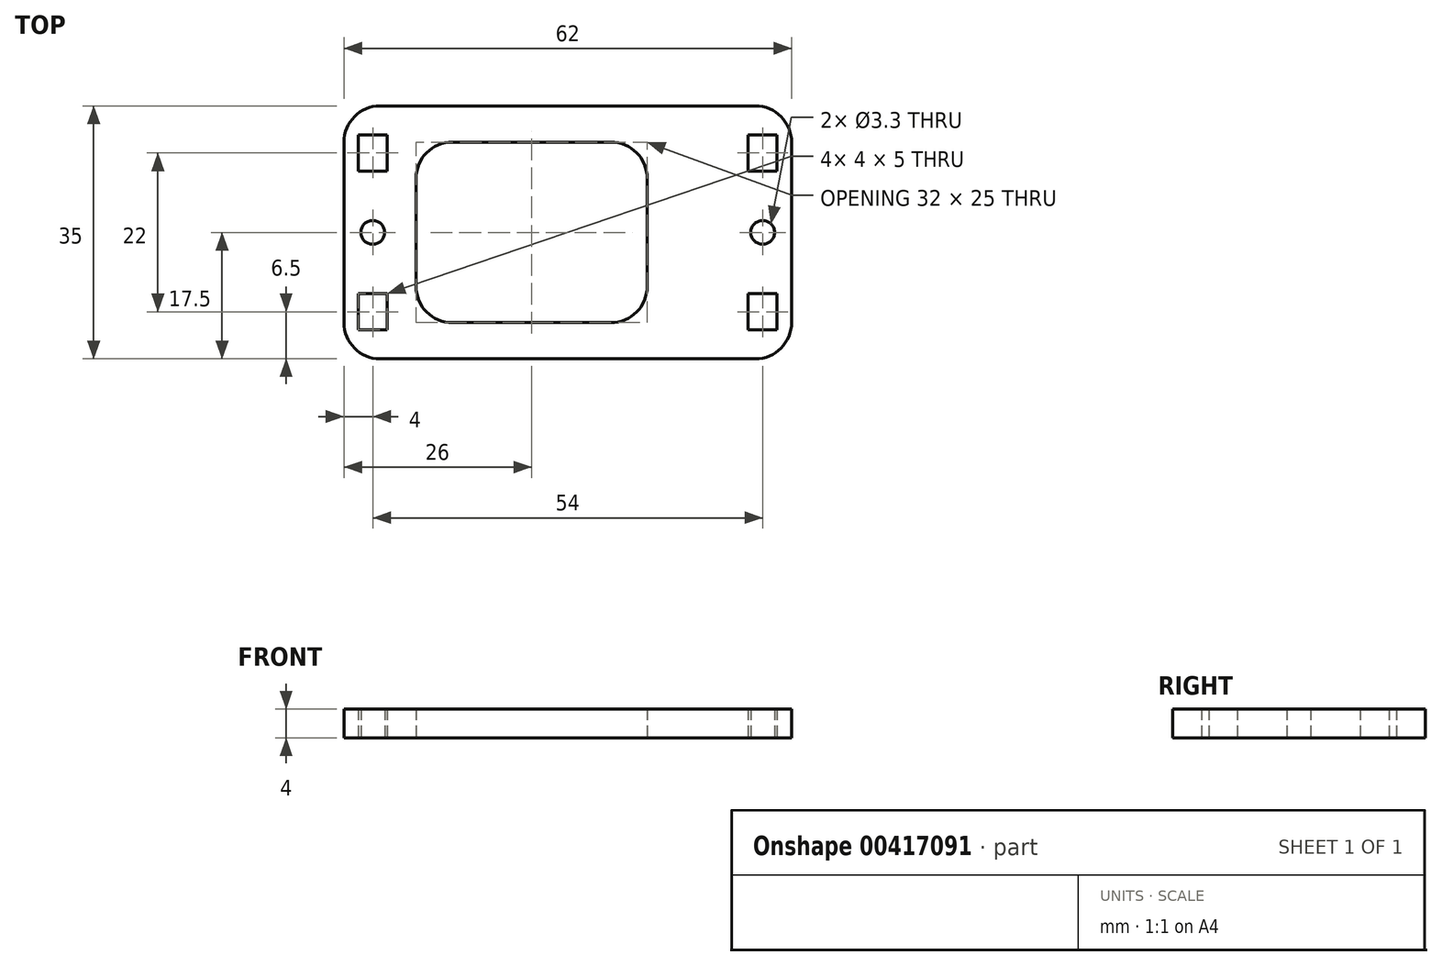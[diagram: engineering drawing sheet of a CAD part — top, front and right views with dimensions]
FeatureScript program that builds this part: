
annotation { "Feature Type Name" : "Feature", "Feature Type Description" : "" }
export const myFeature = defineFeature(function(context is Context, id is Id, definition is map)
    precondition{}
    {
        {
            var Q0;
            Q0=qCreatedBy(makeId("Top.planeOp"),FACE);
            var sketch = newSketch(context, id + "F0", { "sketchPlane" : qUnion([Q0])});
            skLineSegment(sketch, "E0.bottom", {"start": v(31, -17.5) * mm, "end": v(-31, -17.5) * mm});
            skLineSegment(sketch, "E0.top", {"start": v(31, 17.5) * mm, "end": v(-31, 17.5) * mm});
            skLineSegment(sketch, "E0.left", {"start": v(31, -17.5) * mm, "end": v(31, 17.5) * mm});
            skLineSegment(sketch, "E0.right", {"start": v(-31, -17.5) * mm, "end": v(-31, 17.5) * mm});
            skPoint(sketch, "E0.middle", {"position": v(0, 0) * mm});
            skLineSegment(sketch, "E1.bottom", {"start": v(-25, 8.5) * mm, "end": v(-29, 8.5) * mm});
            skLineSegment(sketch, "E1.top", {"start": v(-25, 13.5) * mm, "end": v(-29, 13.5) * mm});
            skLineSegment(sketch, "E1.left", {"start": v(-25, 8.5) * mm, "end": v(-25, 13.5) * mm});
            skLineSegment(sketch, "E1.right", {"start": v(-29, 8.5) * mm, "end": v(-29, 13.5) * mm});
            skPoint(sketch, "E1.middle", {"position": v(-27, 11) * mm});
            skLineSegment(sketch, "E2.MirrorCS", {"start": v(-29, -8.5) * mm, "end": v(-29, -13.5) * mm});
            skLineSegment(sketch, "E3.MirrorCS", {"start": v(-25, -8.5) * mm, "end": v(-25, -13.5) * mm});
            skLineSegment(sketch, "E4.MirrorCS", {"start": v(-25, -8.5) * mm, "end": v(-29, -8.5) * mm});
            skLineSegment(sketch, "E5.MirrorCS", {"start": v(-25, -13.5) * mm, "end": v(-29, -13.5) * mm});
            skPoint(sketch, "E6.MirrorP", {"position": v(-27, -11) * mm});
            skPoint(sketch, "E7.MirrorP", {"position": v(27, 11) * mm});
            skPoint(sketch, "E8.MirrorP", {"position": v(27, -11) * mm});
            skLineSegment(sketch, "E9.MirrorCS", {"start": v(25, -13.5) * mm, "end": v(29, -13.5) * mm});
            skLineSegment(sketch, "E10.MirrorCS", {"start": v(25, -8.5) * mm, "end": v(29, -8.5) * mm});
            skLineSegment(sketch, "E11.MirrorCS", {"start": v(25, -8.5) * mm, "end": v(25, -13.5) * mm});
            skLineSegment(sketch, "E12.MirrorCS", {"start": v(25, 8.5) * mm, "end": v(29, 8.5) * mm});
            skLineSegment(sketch, "E13.MirrorCS", {"start": v(29, -8.5) * mm, "end": v(29, -13.5) * mm});
            skLineSegment(sketch, "E14.MirrorCS", {"start": v(29, 8.5) * mm, "end": v(29, 13.5) * mm});
            skLineSegment(sketch, "E15.MirrorCS", {"start": v(25, 8.5) * mm, "end": v(25, 13.5) * mm});
            skLineSegment(sketch, "E16.MirrorCS", {"start": v(25, 13.5) * mm, "end": v(29, 13.5) * mm});
            skPoint(sketch, "E17", {"position": v(-27, 0) * mm});
            skPoint(sketch, "E18.MirrorP", {"position": v(27, 0) * mm});
            skLineSegment(sketch, "E19.bottom", {"start": v(11, -12.5) * mm, "end": v(-21, -12.5) * mm});
            skLineSegment(sketch, "E19.top", {"start": v(11, 12.5) * mm, "end": v(-21, 12.5) * mm});
            skLineSegment(sketch, "E19.left", {"start": v(11, -12.5) * mm, "end": v(11, 12.5) * mm});
            skLineSegment(sketch, "E19.right", {"start": v(-21, -12.5) * mm, "end": v(-21, 12.5) * mm});
            skPoint(sketch, "E19.middle", {"position": v(-5, 0) * mm});
            skSolve(sketch);
        }
        {
            var Q0;
            Q0=makeQuery(id+"F0.imprint","IMPRINT",FACE,{"disambiguationData":[TD([[makeQuery(id+"F0.imprint","IMPRINT",EDGE,{"derivedFrom":sQuery(id+"F0.wireOp",EDGE,"E0.bottom")}),-1.0]])]});
            extrude(context, id + "F1", {"entities" : qUnion([Q0]), "depth" : 4 * mm});
        }
        {
            var Q0;
            Q0=sQuery(id+"F0.wireOp",VERTEX,"E17");
            var Q1;
            Q1=sQuery(id+"F0.wireOp",VERTEX,"E18.MirrorP");
            var Q2;
            Q2=makeQuery(id+"F1.opExtrude","SWEPT_BODY",BODY,{"disambiguationData":[OSD([sQuery(id+"F0.wireOp",EDGE,"E0.bottom"),sQuery(id+"F0.wireOp",EDGE,"E0.top"),sQuery(id+"F0.wireOp",EDGE,"E0.left"),sQuery(id+"F0.wireOp",EDGE,"E0.right"),sQuery(id+"F0.wireOp",EDGE,"E1.bottom"),sQuery(id+"F0.wireOp",EDGE,"E1.top"),sQuery(id+"F0.wireOp",EDGE,"E1.left"),sQuery(id+"F0.wireOp",EDGE,"E1.right"),sQuery(id+"F0.wireOp",EDGE,"E2.MirrorCS"),sQuery(id+"F0.wireOp",EDGE,"E3.MirrorCS"),sQuery(id+"F0.wireOp",EDGE,"E4.MirrorCS"),sQuery(id+"F0.wireOp",EDGE,"E5.MirrorCS"),sQuery(id+"F0.wireOp",EDGE,"E9.MirrorCS"),sQuery(id+"F0.wireOp",EDGE,"E10.MirrorCS"),sQuery(id+"F0.wireOp",EDGE,"E11.MirrorCS"),sQuery(id+"F0.wireOp",EDGE,"E12.MirrorCS"),sQuery(id+"F0.wireOp",EDGE,"E13.MirrorCS"),sQuery(id+"F0.wireOp",EDGE,"E14.MirrorCS"),sQuery(id+"F0.wireOp",EDGE,"E15.MirrorCS"),sQuery(id+"F0.wireOp",EDGE,"E16.MirrorCS"),sQuery(id+"F0.wireOp",EDGE,"E19.bottom"),sQuery(id+"F0.wireOp",EDGE,"E19.top"),sQuery(id+"F0.wireOp",EDGE,"E19.left"),sQuery(id+"F0.wireOp",EDGE,"E19.right")])]});
            hole(context, id + "F2", {"style" : HoleStyle.SIMPLE, "endStyle" : HoleEndStyle.THROUGH, "oppositeDirection" : true, "standardTappedOrClearance" : lookupTablePath({ "standard" : "ISO", "fit" : "Normal", "size" : "M3", "type" : "Clearance" }), "standardBlindInLast" : lookupTablePath({ "fit" : "Standard", "standard" : "ISO", "size" : "M3", "type" : "Clearance" }), "holeDiameter" : 3.3 * mm, "isTappedThrough" : true, "tappedDepth" : 12 * mm, "tapClearance" : 3, "startFromSketch" : true, "locations" : qUnion([Q0, Q1]), "scope" : qUnion([Q2])});
        }
        {
            var Q0;
            Q0=makeQuery(id+"F1.opExtrude","SWEPT_EDGE",EDGE,{"disambiguationData":[OSD([sQuery(id+"F0.wireOp",EDGE,"E0.bottom"),sQuery(id+"F0.wireOp",EDGE,"E0.right")])]});
            var Q1;
            Q1=makeQuery(id+"F1.opExtrude","SWEPT_EDGE",EDGE,{"disambiguationData":[OSD([sQuery(id+"F0.wireOp",EDGE,"E0.bottom"),sQuery(id+"F0.wireOp",EDGE,"E0.left")])]});
            var Q2;
            Q2=makeQuery(id+"F1.opExtrude","SWEPT_EDGE",EDGE,{"disambiguationData":[OSD([sQuery(id+"F0.wireOp",EDGE,"E0.top"),sQuery(id+"F0.wireOp",EDGE,"E0.left")])]});
            var Q3;
            Q3=makeQuery(id+"F1.opExtrude","SWEPT_EDGE",EDGE,{"disambiguationData":[OSD([sQuery(id+"F0.wireOp",EDGE,"E0.top"),sQuery(id+"F0.wireOp",EDGE,"E0.right")])]});
            fillet(context, id + "F3", {"entities" : qUnion([Q0, Q1, Q2, Q3]), "radius" : 5 * mm, "tangentPropagation" : true, "allowEdgeOverflow" : false});
        }
        {
            var Q0;
            Q0=makeQuery(id+"F1.opExtrude","SWEPT_EDGE",EDGE,{"disambiguationData":[OSD([sQuery(id+"F0.wireOp",EDGE,"E19.top"),sQuery(id+"F0.wireOp",EDGE,"E19.right")])]});
            var Q1;
            Q1=makeQuery(id+"F1.opExtrude","SWEPT_EDGE",EDGE,{"disambiguationData":[OSD([sQuery(id+"F0.wireOp",EDGE,"E19.top"),sQuery(id+"F0.wireOp",EDGE,"E19.left")])]});
            var Q2;
            Q2=makeQuery(id+"F1.opExtrude","SWEPT_EDGE",EDGE,{"disambiguationData":[OSD([sQuery(id+"F0.wireOp",EDGE,"E19.bottom"),sQuery(id+"F0.wireOp",EDGE,"E19.left")])]});
            var Q3;
            Q3=makeQuery(id+"F1.opExtrude","SWEPT_EDGE",EDGE,{"disambiguationData":[OSD([sQuery(id+"F0.wireOp",EDGE,"E19.bottom"),sQuery(id+"F0.wireOp",EDGE,"E19.right")])]});
            fillet(context, id + "F4", {"entities" : qUnion([Q0, Q1, Q2, Q3]), "radius" : 5 * mm, "tangentPropagation" : true, "allowEdgeOverflow" : false});
        }
    });
